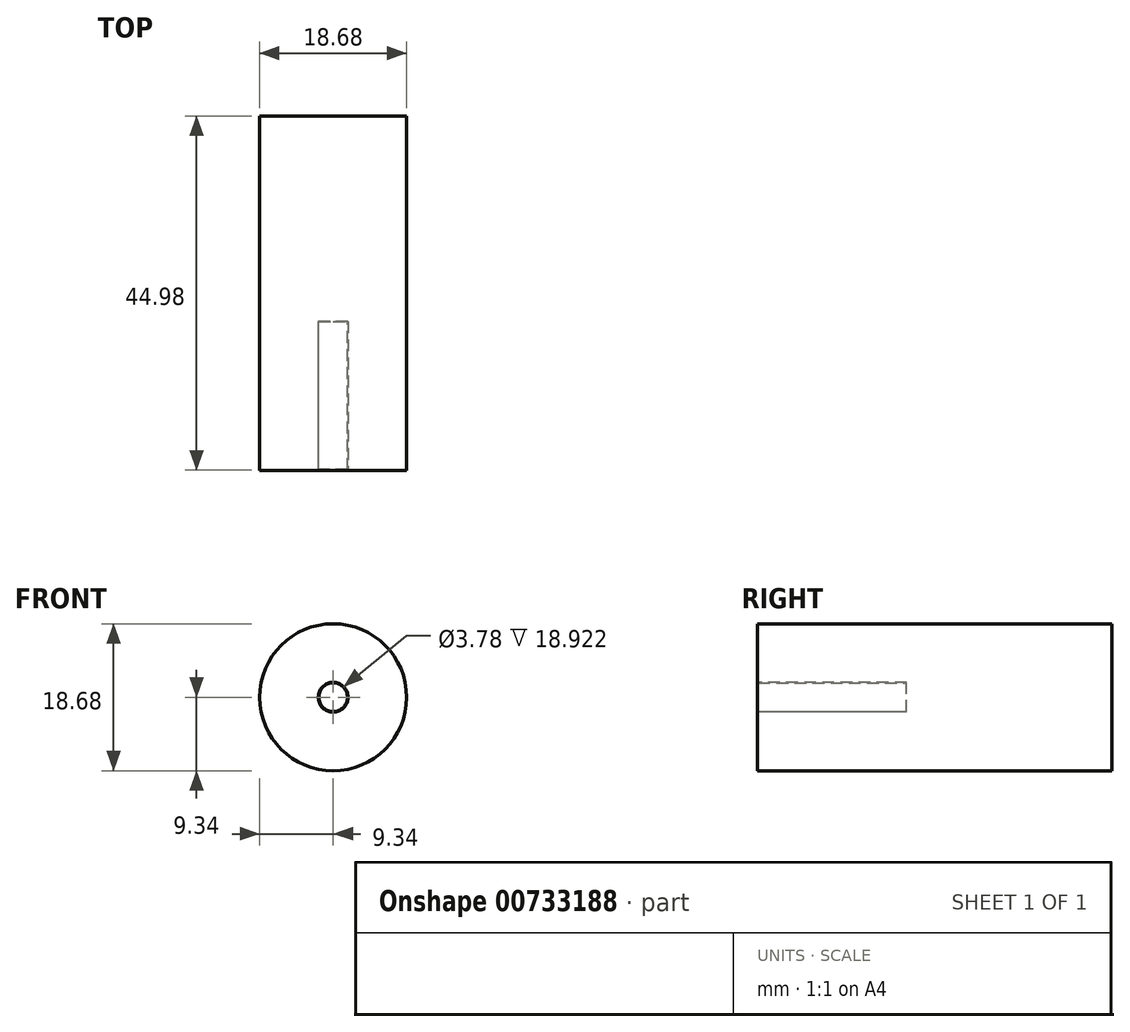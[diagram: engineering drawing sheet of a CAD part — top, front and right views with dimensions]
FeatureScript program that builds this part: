
annotation { "Feature Type Name" : "Feature", "Feature Type Description" : "" }
export const myFeature = defineFeature(function(context is Context, id is Id, definition is map)
    precondition{}
    {
        {
            var Q0;
            Q0=qCreatedBy(makeId("Front.planeOp"),FACE);
            var sketch = newSketch(context, id + "F0", { "sketchPlane" : qUnion([Q0])});
            skCircle(sketch, "E0", {"center": v(0, 0) * mm, "radius": 9.34 * mm});
            skSolve(sketch);
        }
        {
            var Q0;
            Q0 = qSketchRegion(id + "F0", true);
            extrude(context, id + "F1", {"entities" : qUnion([Q0]), "oppositeDirection" : true, "depth" : 23.9 * mm, "offsetDistance" : 25.4 * mm, "hasSecondDirection" : true, "secondDirectionOppositeDirection" : false, "secondDirectionDepth" : 21.08 * mm});
        }
        {
            var Q0;
            Q0=makeQuery(id+"F1.opExtrude","CAP_FACE",FACE,{"disambiguationData":[OSD([sQuery(id+"F0.wireOp",EDGE,"E0")])],"isStart":true});
            var sketch = newSketch(context, id + "F2", { "sketchPlane" : qUnion([Q0])});
            skCircle(sketch, "E1", {"center": v(0, 0) * mm, "radius": 1.9 * mm});
            skSolve(sketch);
        }
        {
            var Q0;
            Q0 = qSketchRegion(id + "F2", true);
            extrude(context, id + "F3", {"entities" : qUnion([Q0]), "operationType" : NewBodyOperationType.REMOVE, "oppositeDirection" : true, "depth" : 18.92 * mm, "offsetDistance" : 25.4 * mm});
        }
        {
            var Q0;
            Q0=makeQuery(id+"F3.boolean.opBoolean","COPY",FACE,{"derivedFrom":makeQuery(id+"F3.opExtrude","CAP_FACE",FACE,{"disambiguationData":[OSD([sQuery(id+"F2.wireOp",EDGE,"E1")])],"isStart":false})});
            var sketch = newSketch(context, id + "F4", { "sketchPlane" : qUnion([Q0])});
            skCircle(sketch, "E2", {"center": v(0, 0) * mm, "radius": 1.83 * mm});
            skSolve(sketch);
        }
        {
            var Q0;
            Q0 = qSketchRegion(id + "F4", true);
            extrude(context, id + "F5", {"entities" : qUnion([Q0]), "depth" : 18.83 * mm, "offsetDistance" : 25.4 * mm});
        }
    });
